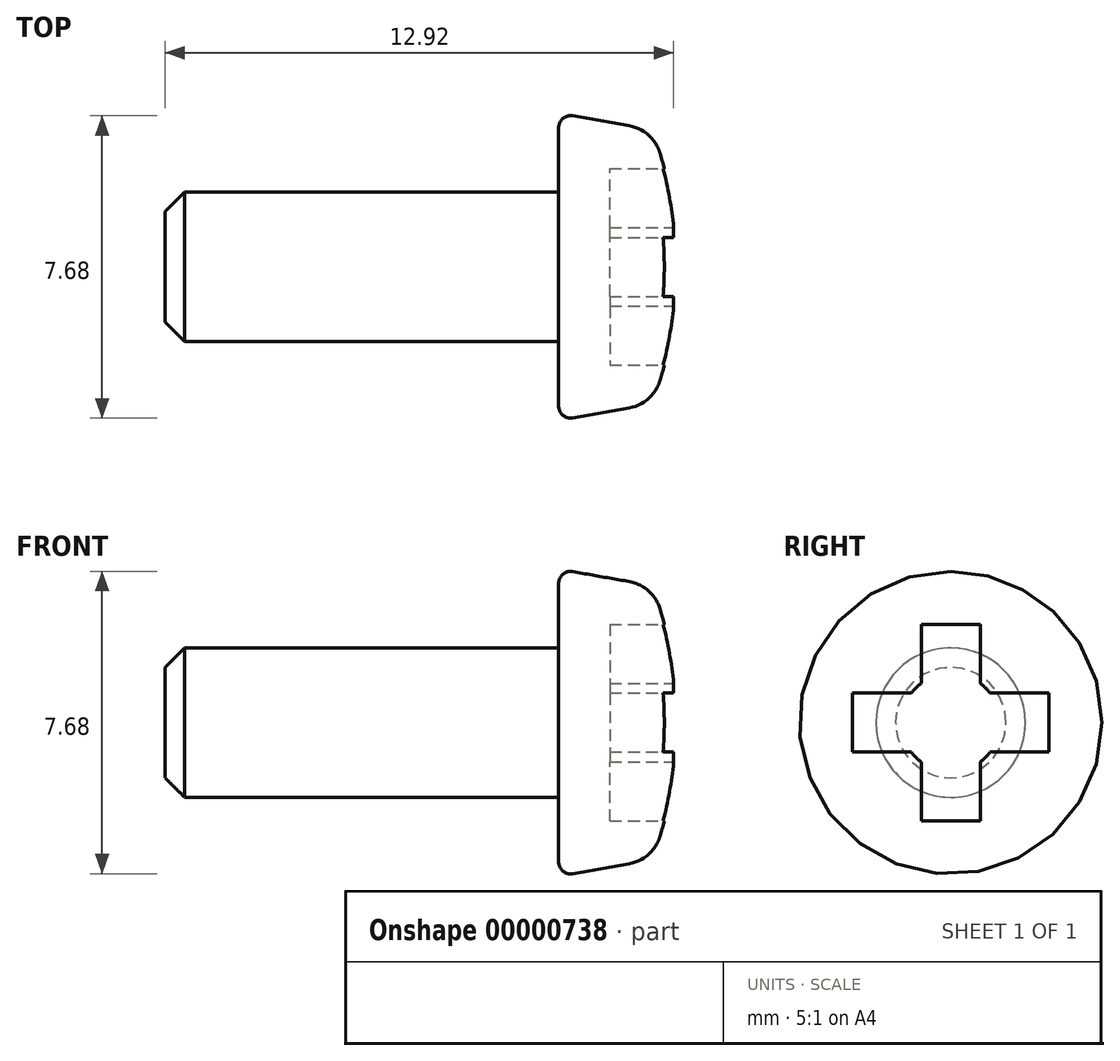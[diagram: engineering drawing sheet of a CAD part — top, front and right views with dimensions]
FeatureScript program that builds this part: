
annotation { "Feature Type Name" : "Feature", "Feature Type Description" : "" }
export const myFeature = defineFeature(function(context is Context, id is Id, definition is map)
    precondition{}
    {
        {
            var Q0;
            Q0=qCreatedBy(makeId("Front.planeOp"),FACE);
            var sketch = newSketch(context, id + "F0", { "sketchPlane" : qUnion([Q0])});
            skLineSegment(sketch, "E0", {"start": v(0, 1.9) * mm, "end": v(-10, 1.9) * mm});
            skLineSegment(sketch, "E1", {"start": v(-10, 1.9) * mm, "end": v(-10, 0) * mm});
            skLineSegment(sketch, "E2", {"start": v(-10, 0) * mm, "end": v(3, 0) * mm});
            skLineSegment(sketch, "E3", {"start": v(0, 1.9) * mm, "end": v(0, 3.9) * mm});
            skLineSegment(sketch, "E4", {"start": v(0, 3.9) * mm, "end": v(2.37, 3.48) * mm});
            skArc(sketch, "E5", {"start": v(3, 0) * mm, "mid": v(2.84, 1.77) * mm, "end": v(2.37, 3.48) * mm});
            skLineSegment(sketch, "E6", {"start": v(0, 0) * mm, "end": v(12.4, 0) * mm, "construction": true});
            skSolve(sketch);
        }
        {
            var Q0;
            Q0=makeQuery(id+"F0.imprint","IMPRINT",FACE,{"disambiguationData":[TD([[makeQuery(id+"F0.imprint","IMPRINT",EDGE,{"derivedFrom":sQuery(id+"F0.wireOp",EDGE,"E0")}),1.0]])]});
            var Q1;
            Q1=sQuery(id+"F0.wireOp",EDGE,"E6");
            revolve(context, id + "F1", {"entities" : qUnion([Q0]), "axis" : qUnion([Q1]), "revolveType" : RevolveType.FULL});
        }
        {
            var Q0;
            Q0=makeQuery(id+"F1.opRevolve","SWEPT_EDGE",EDGE,{"disambiguationData":[OSD([sQuery(id+"F0.wireOp",EDGE,"E0"),sQuery(id+"F0.wireOp",EDGE,"E1")])]});
            chamfer(context, id + "F2", {"entities" : qUnion([Q0]), "width" : .5 * mm, "tangentPropagation" : true});
        }
        {
            var Q0;
            Q0=makeQuery(id+"F1.opRevolve","SWEPT_EDGE",EDGE,{"disambiguationData":[OSD([sQuery(id+"F0.wireOp",EDGE,"E4"),sQuery(id+"F0.wireOp",EDGE,"E5")])]});
            fillet(context, id + "F3", {"entities" : qUnion([Q0]), "radius" : 1 * mm, "tangentPropagation" : true, "allowEdgeOverflow" : false});
        }
        {
            var Q0;
            Q0=makeQuery(id+"F1.opRevolve","SWEPT_EDGE",EDGE,{"disambiguationData":[OSD([sQuery(id+"F0.wireOp",EDGE,"E3"),sQuery(id+"F0.wireOp",EDGE,"E4")])]});
            fillet(context, id + "F4", {"entities" : qUnion([Q0]), "radius" : .3 * mm, "tangentPropagation" : true, "allowEdgeOverflow" : false});
        }
        {
            var Q0;
            Q0=qCreatedBy(makeId("Right.planeOp"),FACE);
            cPlane(context, id + "F5", {"entities" : qUnion([Q0]), "cplaneType" : CPlaneType.OFFSET, "offset" : 3 * mm, "width" : 150 * mm, "height" : 150 * mm});
        }
        {
            var Q0;
            Q0=qCreatedBy(id+"F5.planeOp",FACE);
            var sketch = newSketch(context, id + "F6", { "sketchPlane" : qUnion([Q0])});
            skLineSegment(sketch, "E7", {"start": v(0, 2.5) * mm, "end": v(0.75, 2.5) * mm});
            skLineSegment(sketch, "E8", {"start": v(0.75, 2.5) * mm, "end": v(0.75, 1) * mm});
            skLineSegment(sketch, "E9", {"start": v(1, 0.75) * mm, "end": v(2.5, 0.75) * mm});
            skLineSegment(sketch, "E10", {"start": v(2.5, 0.75) * mm, "end": v(2.5, 0) * mm});
            skArc(sketch, "E11", {"start": v(1, 0.75) * mm, "mid": v(0.88, 0.88) * mm, "end": v(0.75, 1) * mm});
            skLineSegment(sketch, "E12", {"start": v(0, 0) * mm, "end": v(0, 2.5) * mm, "construction": true});
            skLineSegment(sketch, "E13", {"start": v(0, 0) * mm, "end": v(2.56, 0) * mm, "construction": true});
            skLineSegment(sketch, "E14.0.MirrorCS", {"start": v(0, 2.5) * mm, "end": v(-0.75, 2.5) * mm});
            skLineSegment(sketch, "E15.0.MirrorCS", {"start": v(-0.75, 2.5) * mm, "end": v(-0.75, 1) * mm});
            skArc(sketch, "E16.0.MirrorCS", {"start": v(-1, 0.75) * mm, "mid": v(-0.88, 0.88) * mm, "end": v(-0.75, 1) * mm});
            skLineSegment(sketch, "E17.0.MirrorCS", {"start": v(-1, 0.75) * mm, "end": v(-2.5, 0.75) * mm});
            skLineSegment(sketch, "E18.0.MirrorCS", {"start": v(-2.5, 0.75) * mm, "end": v(-2.5, 0) * mm});
            skLineSegment(sketch, "E19.0.MirrorCS", {"start": v(-2.5, -0.75) * mm, "end": v(-2.5, 0) * mm});
            skLineSegment(sketch, "E20.0.MirrorCS", {"start": v(-1, -0.75) * mm, "end": v(-2.5, -0.75) * mm});
            skArc(sketch, "E21.0.MirrorCS", {"start": v(-1, -0.75) * mm, "mid": v(-0.88, -0.88) * mm, "end": v(-0.75, -1) * mm});
            skLineSegment(sketch, "E22.0.MirrorCS", {"start": v(-0.75, -2.5) * mm, "end": v(-0.75, -1) * mm});
            skLineSegment(sketch, "E23.0.MirrorCS", {"start": v(0, -2.5) * mm, "end": v(-0.75, -2.5) * mm});
            skLineSegment(sketch, "E24.0.MirrorCS", {"start": v(0, -2.5) * mm, "end": v(0.75, -2.5) * mm});
            skLineSegment(sketch, "E25.0.MirrorCS", {"start": v(0.75, -2.5) * mm, "end": v(0.75, -1) * mm});
            skArc(sketch, "E26.0.MirrorCS", {"start": v(1, -0.75) * mm, "mid": v(0.88, -0.88) * mm, "end": v(0.75, -1) * mm});
            skLineSegment(sketch, "E27.0.MirrorCS", {"start": v(1, -0.75) * mm, "end": v(2.5, -0.75) * mm});
            skLineSegment(sketch, "E28.0.MirrorCS", {"start": v(2.5, -0.75) * mm, "end": v(2.5, 0) * mm});
            skSolve(sketch);
        }
        {
            var Q0;
            Q0=makeQuery(id+"F6.imprint","IMPRINT",FACE,{"disambiguationData":[TD([[makeQuery(id+"F6.imprint","IMPRINT",EDGE,{"derivedFrom":sQuery(id+"F6.wireOp",EDGE,"E7")}),-1.0]])]});
            extrude(context, id + "F7", {"entities" : qUnion([Q0]), "operationType" : NewBodyOperationType.REMOVE, "oppositeDirection" : true, "depth" : 1.7 * mm});
        }
    });
